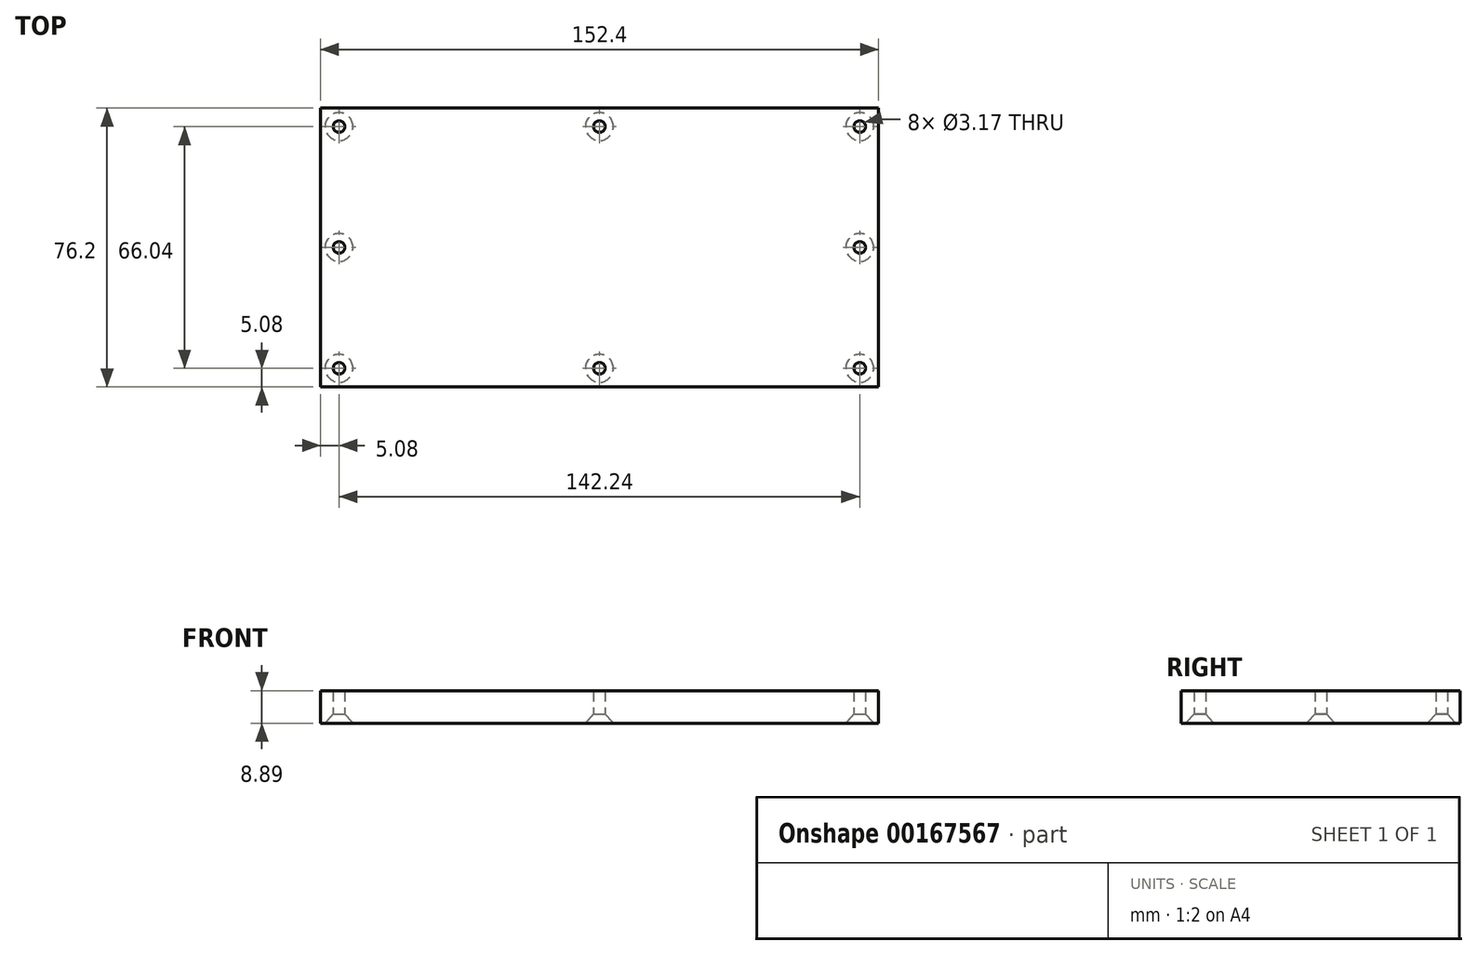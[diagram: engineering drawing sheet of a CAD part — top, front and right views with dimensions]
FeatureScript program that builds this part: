
annotation { "Feature Type Name" : "Feature", "Feature Type Description" : "" }
export const myFeature = defineFeature(function(context is Context, id is Id, definition is map)
    precondition{}
    {
        {
            var Q0;
            Q0=qCreatedBy(makeId("Top.planeOp"),FACE);
            var sketch = newSketch(context, id + "F0", { "sketchPlane" : qUnion([Q0])});
            skLineSegment(sketch, "E0.bottom", {"start": v(0, 0) * mm, "end": v(152.4, 0) * mm});
            skLineSegment(sketch, "E0.top", {"start": v(0, 76.2) * mm, "end": v(152.4, 76.2) * mm});
            skLineSegment(sketch, "E0.left", {"start": v(0, 0) * mm, "end": v(0, 76.2) * mm});
            skLineSegment(sketch, "E0.right", {"start": v(152.4, 0) * mm, "end": v(152.4, 76.2) * mm});
            skSolve(sketch);
        }
        {
            var Q0;
            Q0 = qSketchRegion(id + "F0", true);
            extrude(context, id + "F1", {"entities" : qUnion([Q0]), "depth" : 8.9 * mm});
        }
        {
            var Q0;
            Q0=makeQuery(id+"F1.opExtrude","CAP_FACE",FACE,{"disambiguationData":[OSD([sQuery(id+"F0.wireOp",EDGE,"E0.bottom"),sQuery(id+"F0.wireOp",EDGE,"E0.top"),sQuery(id+"F0.wireOp",EDGE,"E0.left"),sQuery(id+"F0.wireOp",EDGE,"E0.right")])],"isStart":true});
            var sketch = newSketch(context, id + "F2", { "sketchPlane" : qUnion([Q0])});
            skPoint(sketch, "E1", {"position": v(5.08, -5.08) * mm});
            skPoint(sketch, "E2", {"position": v(5.08, -71.12) * mm});
            skPoint(sketch, "E3", {"position": v(147.32, -71.12) * mm});
            skPoint(sketch, "E4", {"position": v(147.32, -5.08) * mm});
            skPoint(sketch, "E5", {"position": v(76.2, -71.12) * mm});
            skPoint(sketch, "E6", {"position": v(76.2, -5.08) * mm});
            skPoint(sketch, "E7", {"position": v(5.08, -38.1) * mm});
            skPoint(sketch, "E8", {"position": v(147.32, -38.1) * mm});
            skSolve(sketch);
        }
        {
            var Q0;
            Q0=sQuery(id+"F2.wireOp",VERTEX,"E1");
            var Q1;
            Q1=sQuery(id+"F2.wireOp",VERTEX,"E7");
            var Q2;
            Q2=sQuery(id+"F2.wireOp",VERTEX,"E2");
            var Q3;
            Q3=sQuery(id+"F2.wireOp",VERTEX,"E5");
            var Q4;
            Q4=sQuery(id+"F2.wireOp",VERTEX,"E3");
            var Q5;
            Q5=sQuery(id+"F2.wireOp",VERTEX,"E8");
            var Q6;
            Q6=sQuery(id+"F2.wireOp",VERTEX,"E4");
            var Q7;
            Q7=sQuery(id+"F2.wireOp",VERTEX,"E6");
            var Q8;
            Q8=makeQuery(id+"F1.opExtrude","SWEPT_BODY",BODY,{"disambiguationData":[OSD([sQuery(id+"F0.wireOp",EDGE,"E0.bottom"),sQuery(id+"F0.wireOp",EDGE,"E0.top"),sQuery(id+"F0.wireOp",EDGE,"E0.left"),sQuery(id+"F0.wireOp",EDGE,"E0.right")])]});
            hole(context, id + "F3", {"style" : HoleStyle.C_SINK, "endStyle" : HoleEndStyle.THROUGH, "holeDiameter" : 3.17 * mm, "cSinkDiameter" : 7.62 * mm, "cSinkAngle" : 82 * degree, "locations" : qUnion([Q0, Q1, Q2, Q3, Q4, Q5, Q6, Q7]), "scope" : qUnion([Q8]), "isTappedThrough" : true});
        }
    });
